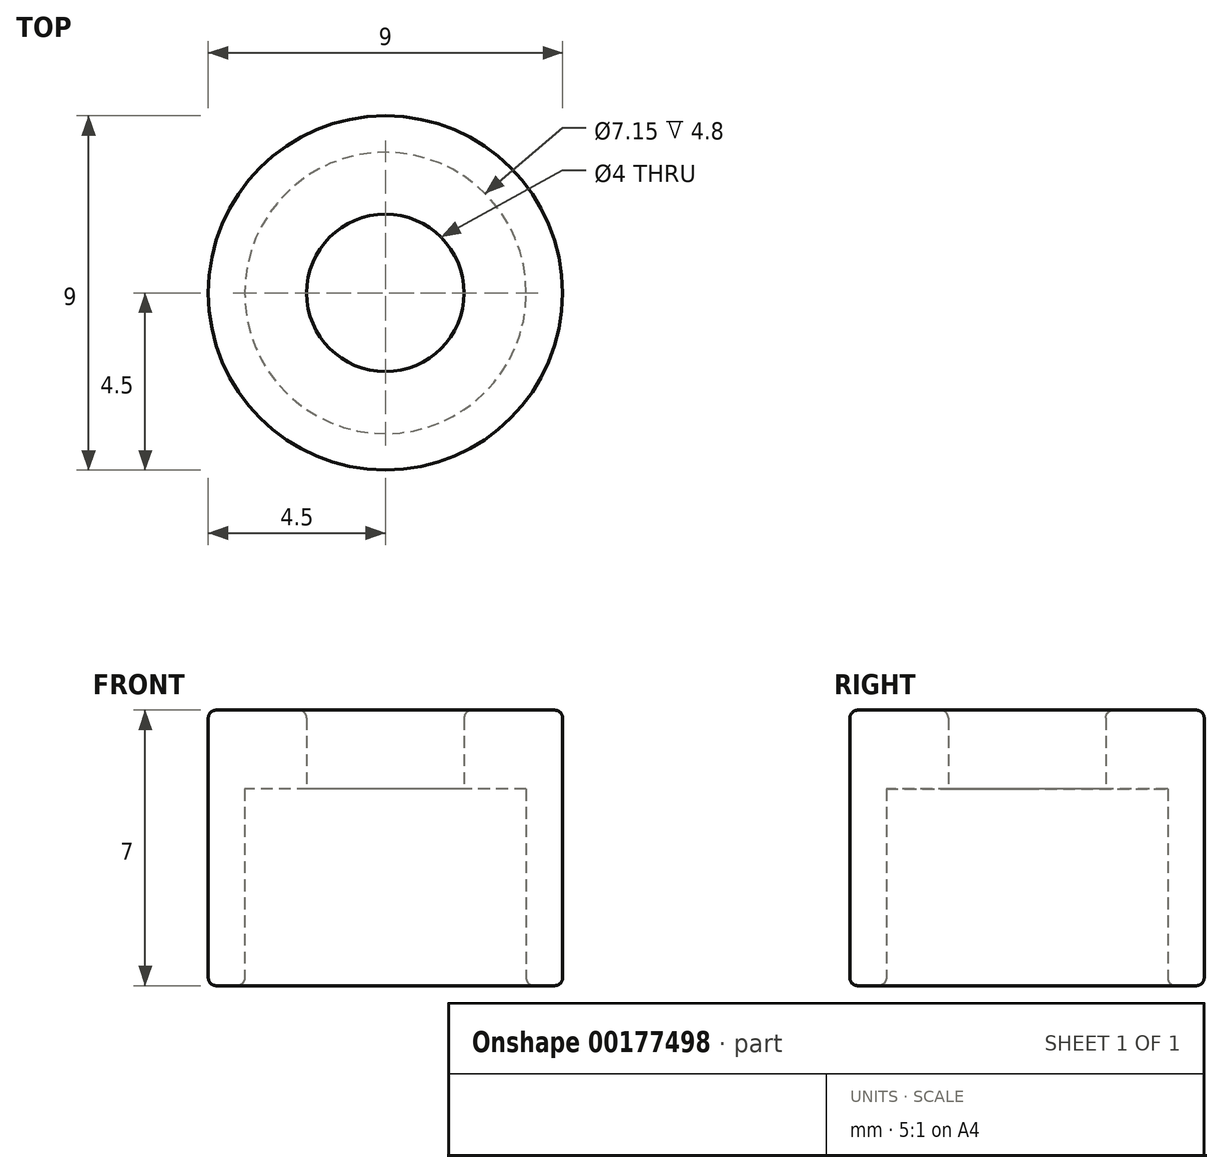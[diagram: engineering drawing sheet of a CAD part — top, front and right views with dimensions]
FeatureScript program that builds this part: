
annotation { "Feature Type Name" : "Feature", "Feature Type Description" : "" }
export const myFeature = defineFeature(function(context is Context, id is Id, definition is map)
    precondition{}
    {
        {
            var Q0;
            Q0=qCreatedBy(makeId("Top.planeOp"),FACE);
            var sketch = newSketch(context, id + "F0", { "sketchPlane" : qUnion([Q0])});
            skCircle(sketch, "E0", {"center": v(0, 0) * mm, "radius": 3.58 * mm});
            skCircle(sketch, "E1", {"center": v(0, 0) * mm, "radius": 4.5 * mm});
            skSolve(sketch);
        }
        {
            var Q0;
            Q0 = qSketchRegion(id + "F0", true);
            extrude(context, id + "F1", {"entities" : qUnion([Q0]), "depth" : 5 * mm});
        }
        {
            var Q0;
            Q0=qCreatedBy(makeId("Front.planeOp"),FACE);
            var sketch = newSketch(context, id + "F2", { "sketchPlane" : qUnion([Q0])});
            skCircle(sketch, "E2", {"center": v(0, 17) * mm, "radius": 5 * mm});
            skLineSegment(sketch, "E3", {"start": v(0, 0) * mm, "end": v(0, 28.03) * mm});
            skSolve(sketch);
        }
        {
            var Q0;
            {var subQ0=sQuery(id+"F2.wireOp",EDGE,"E3");var subQ1=sQuery(id+"F2.wireOp",EDGE,"E2");var subQ2=makeQuery(id+"F2.imprint","INTERSECT",VERTEX,{"disambiguationData":[OD(0.0)],"derivedFrom":[subQ1,subQ0]});Q0=makeQuery(id+"F2.imprint","IMPRINT",FACE,{"disambiguationData":[TD([[makeQuery(id+"F2.imprint","IMPRINT",EDGE,{"disambiguationData":[TD([[subQ2,1.0]])],"derivedFrom":subQ1}),1.0]])]});}
            var Q1;
            Q1=sQuery(id+"F2.wireOp",EDGE,"E3");
            revolve(context, id + "F3", {"operationType" : NewBodyOperationType.REMOVE, "entities" : qUnion([Q0]), "axis" : qUnion([Q1]), "revolveType" : RevolveType.FULL});
        }
        {
            var Q0;
            Q0=makeQuery(id+"F1.opExtrude","CAP_FACE",FACE,{"disambiguationData":[OSD([sQuery(id+"F0.wireOp",EDGE,"E0"),sQuery(id+"F0.wireOp",EDGE,"E1")])],"isStart":false});
            var sketch = newSketch(context, id + "F4", { "sketchPlane" : qUnion([Q0])});
            skCircle(sketch, "E4", {"center": v(0, 0) * mm, "radius": 2 * mm});
            skCircle(sketch, "E5", {"center": v(0, 0) * mm, "radius": 4.5 * mm});
            skSolve(sketch);
        }
        {
            var Q0;
            Q0 = qSketchRegion(id + "F4", true);
            extrude(context, id + "F5", {"entities" : qUnion([Q0]), "operationType" : NewBodyOperationType.ADD, "depth" : 2 * mm});
        }
        {
            var Q0;
            Q0=makeQuery(id+"F3.boolean.opBoolean","INTERSECT",EDGE,{"derivedFrom":[makeQuery(id+"F1.opExtrude","SWEPT_FACE",FACE,{"disambiguationData":[OSD([sQuery(id+"F0.wireOp",EDGE,"E1")])]}),makeQuery(id+"F3.opRevolve","SWEPT_FACE",FACE,{"disambiguationData":[OSD([sQuery(id+"F2.wireOp",EDGE,"E2")])]})]});
            var Q1;
            Q1=makeQuery(id+"F1.opExtrude","CAP_EDGE",EDGE,{"disambiguationData":[OSD([sQuery(id+"F0.wireOp",EDGE,"E1")])],"isStart":true});
            var Q2;
            Q2=makeQuery(id+"F5.opExtrude","CAP_EDGE",EDGE,{"disambiguationData":[OSD([sQuery(id+"F4.wireOp",EDGE,"E4")])],"isStart":false});
            var Q3;
            Q3=makeQuery(id+"F5.opExtrude","CAP_EDGE",EDGE,{"disambiguationData":[OSD([sQuery(id+"F4.wireOp",EDGE,"E5")])],"isStart":false});
            var Q4;
            Q4=makeQuery(id+"F1.opExtrude","CAP_EDGE",EDGE,{"disambiguationData":[OSD([sQuery(id+"F0.wireOp",EDGE,"E0")])],"isStart":true});
            fillet(context, id + "F6", {"entities" : qUnion([Q0, Q1, Q2, Q3, Q4]), "radius" : 0.2 * mm, "tangentPropagation" : true, "allowEdgeOverflow" : false});
        }
    });
